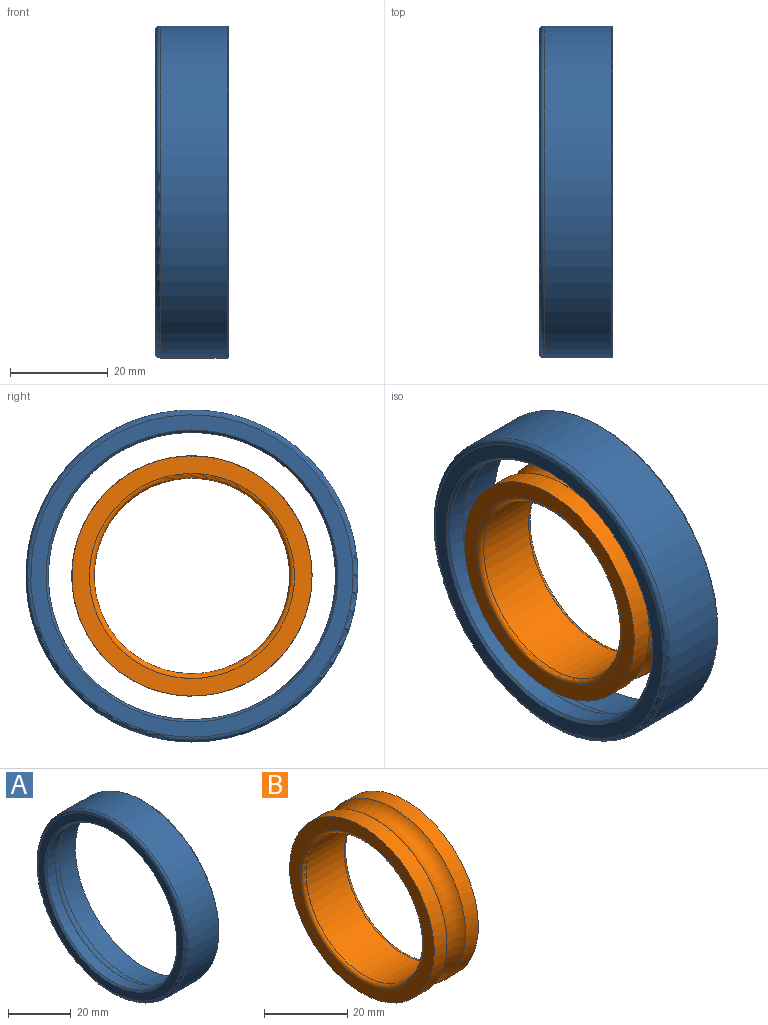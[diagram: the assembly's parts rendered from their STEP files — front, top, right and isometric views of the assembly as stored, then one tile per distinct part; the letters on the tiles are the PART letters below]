
ASSEMBLY  parts=2 mates=1
PART A: 9 faces, bbox 15x73.6x73.6 mm
  f0: plane 67.4x67.4mm, normal (1,0,0), area 529mm2, adj f1,f2
  f1: cone r=0mm half-angle=1deg, axis (1,0,0), area 1476.1mm2, adj f0,f3
  f2: torus R=33.7mm, axis (1,0,0), area 100.3mm2, adj f0,f4
  f3: torus R=27mm, axis (1,0,0), area 685.8mm2, adj f1,f5
  f4: cylinder r=34mm len=68mm, axis (1,0,0), area 2926.7mm2, adj f2,f6
  f5: cylinder r=29.4mm len=58.8mm, axis (1,0,0), area 709.1mm2, adj f3,f7
  f6: torus R=33mm, axis (1,0,0), area 332mm2, adj f4,f8
  f7: cone r=0mm half-angle=45deg, axis (-1,0,0), area 131.7mm2, adj f5,f8
  f8: plane 66x66mm, normal (-1,0,0), area 612.9mm2, adj f6,f7
PART B: 8 faces, bbox 15x58.4x58.4 mm
  f0: torus R=21mm, axis (1,0,0), area 201mm2, adj f1,f2
  f1: cylinder r=20mm len=40mm, axis (1,0,0), area 1633.6mm2, adj f0,f3
  f2: plane 49.2x49.2mm, normal (-1,0,0), area 515.6mm2, adj f0,f4
  f3: torus R=21mm, axis (1,0,0), area 201mm2, adj f1,f5
  f4: cylinder r=24.6mm len=49.2mm, axis (1,0,0), area 670.6mm2, adj f2,f7
  f5: plane 49.2x49.2mm, normal (1,0,0), area 515.8mm2, adj f3,f6
  f6: cylinder r=24.6mm len=49.2mm, axis (1,0,0), area 670.6mm2, adj f5,f7
  f7: torus R=27mm, axis (1,0,0), area 1083.2mm2, adj f4,f6
PLACE A at identity fixed
PLACE B rot(axis=(-1,0,0),97.3deg) t=(0,0,0)mm
MATE revolute A.f1 <-> B.f0  axis (1,0,0) through (15,0,0)mm
